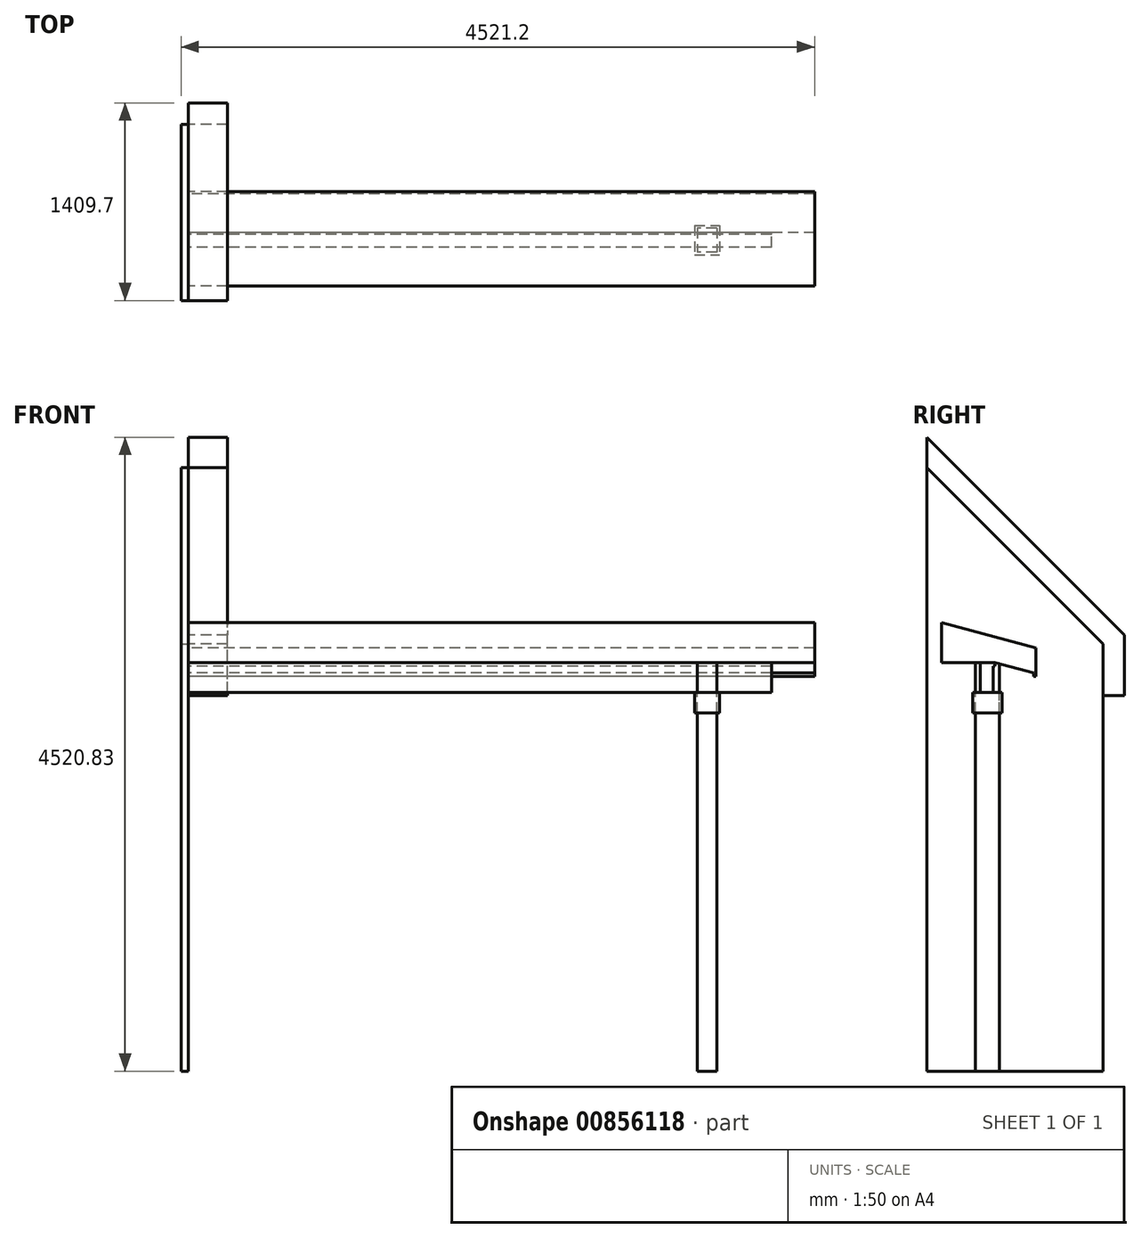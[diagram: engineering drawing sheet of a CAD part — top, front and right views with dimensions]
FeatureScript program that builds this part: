
annotation { "Feature Type Name" : "Feature", "Feature Type Description" : "" }
export const myFeature = defineFeature(function(context is Context, id is Id, definition is map)
    precondition{}
    {
        {
            var Q0;
            Q0=qCreatedBy(makeId("Right.planeOp"),FACE);
            var sketch = newSketch(context, id + "F0", { "sketchPlane" : qUnion([Q0])});
            skLineSegment(sketch, "E0.bottom", {"start": v(0, 2701.93) * mm, "end": v(92.07, 2701.93) * mm});
            skLineSegment(sketch, "E0.top", {"start": v(0, 2914.65) * mm, "end": v(104.77, 2914.65) * mm});
            skLineSegment(sketch, "E0.left", {"start": v(0, 2701.93) * mm, "end": v(0, 2914.65) * mm});
            skLineSegment(sketch, "E0.right", {"start": v(92.07, 2701.93) * mm, "end": v(92.07, 2889.25) * mm});
            skLineSegment(sketch, "E1", {"start": v(92.07, 2889.25) * mm, "end": v(104.77, 2889.25) * mm});
            skLineSegment(sketch, "E2", {"start": v(104.77, 2889.25) * mm, "end": v(104.77, 2889.25) * mm});
            skLineSegment(sketch, "E3", {"start": v(104.77, 2889.25) * mm, "end": v(104.77, 2914.65) * mm});
            skSolve(sketch);
        }
        {
            var Q0;
            Q0 = qSketchRegion(id + "F0", true);
            extrude(context, id + "F1", {"entities" : qUnion([Q0]), "depth" : 4162.43 * mm, "offsetDistance" : 25.4 * mm});
        }
        {
            var Q0;
            Q0=makeQuery(id+"F1.opExtrude","SWEPT_FACE",FACE,{"disambiguationData":[OSD([sQuery(id+"F0.wireOp",EDGE,"E0.top")])]});
            var sketch = newSketch(context, id + "F2", { "sketchPlane" : qUnion([Q0])});
            skLineSegment(sketch, "E4.bottom", {"start": v(3632.2, -34.93) * mm, "end": v(3771.9, -34.93) * mm});
            skLineSegment(sketch, "E4.top", {"start": v(3632.2, 136.52) * mm, "end": v(3771.9, 136.52) * mm});
            skLineSegment(sketch, "E4.left", {"start": v(3632.2, -34.93) * mm, "end": v(3632.2, 136.52) * mm});
            skLineSegment(sketch, "E4.right", {"start": v(3771.9, -34.93) * mm, "end": v(3771.9, 136.52) * mm});
            skSolve(sketch);
        }
        {
            var Q0;
            Q0 = qSketchRegion(id + "F2", true);
            var Q1;
            Q1=qCreatedBy(makeId("Top.planeOp"),FACE);
            extrude(context, id + "F3", {"entities" : qUnion([Q0]), "endBound" : BoundingType.UP_TO_SURFACE, "oppositeDirection" : true, "depth" : 25.4 * mm, "endBoundEntityFace" : qUnion([Q1]), "offsetDistance" : 25.4 * mm});
        }
        {
            var Q0;
            Q0=qCreatedBy(makeId("Right.planeOp"),FACE);
            var sketch = newSketch(context, id + "F4", { "sketchPlane" : qUnion([Q0])});
            skLineSegment(sketch, "E5", {"start": v(104.77, 2914.65) * mm, "end": v(380.79, 2840.7) * mm});
            skLineSegment(sketch, "E6", {"start": v(380.79, 2840.7) * mm, "end": v(380.79, 2815.3) * mm});
            skLineSegment(sketch, "E7", {"start": v(380.79, 2815.3) * mm, "end": v(396.66, 2815.3) * mm});
            skLineSegment(sketch, "E8", {"start": v(396.66, 2815.3) * mm, "end": v(396.66, 3018.5) * mm});
            skLineSegment(sketch, "E9", {"start": v(396.66, 3018.5) * mm, "end": v(-276.23, 3198.8) * mm});
            skLineSegment(sketch, "E10", {"start": v(-276.23, 2914.65) * mm, "end": v(104.77, 2914.65) * mm});
            skLineSegment(sketch, "E11", {"start": v(-276.23, 3198.8) * mm, "end": v(-276.23, 2914.65) * mm});
            skSolve(sketch);
        }
        {
            var Q0;
            Q0 = qSketchRegion(id + "F4", true);
            extrude(context, id + "F5", {"entities" : qUnion([Q0]), "depth" : 4470.4 * mm, "offsetDistance" : 25.4 * mm});
        }
        {
            var Q0;
            Q0=makeQuery(id+"F1.opExtrude","SWEPT_FACE",FACE,{"disambiguationData":[OSD([sQuery(id+"F0.wireOp",EDGE,"E0.bottom")])]});
            var sketch = newSketch(context, id + "F6", { "sketchPlane" : qUnion([Q0])});
            skLineSegment(sketch, "E12.bottom", {"start": v(3613.15, -155.57) * mm, "end": v(3790.95, -155.57) * mm});
            skLineSegment(sketch, "E12.top", {"start": v(3613.15, 53.98) * mm, "end": v(3790.95, 53.98) * mm});
            skLineSegment(sketch, "E12.left", {"start": v(3613.15, -155.57) * mm, "end": v(3613.15, 53.98) * mm});
            skLineSegment(sketch, "E12.right", {"start": v(3790.95, -155.57) * mm, "end": v(3790.95, 53.98) * mm});
            skSolve(sketch);
        }
        {
            var Q0;
            Q0 = qSketchRegion(id + "F6", true);
            extrude(context, id + "F7", {"entities" : qUnion([Q0]), "depth" : 147.32 * mm, "offsetDistance" : 25.4 * mm});
        }
        {
            var Q0;
            Q0=qCreatedBy(makeId("Right.planeOp"),FACE);
            var sketch = newSketch(context, id + "F8", { "sketchPlane" : qUnion([Q0])});
            skLineSegment(sketch, "E13", {"start": v(876.3, 0) * mm, "end": v(876.3, 3048) * mm});
            skLineSegment(sketch, "E14", {"start": v(876.3, 3048) * mm, "end": v(-381, 4305.3) * mm});
            skLineSegment(sketch, "E15", {"start": v(-381, 4305.3) * mm, "end": v(-381, 0) * mm});
            skLineSegment(sketch, "E16", {"start": v(-381, 0) * mm, "end": v(876.3, 0) * mm});
            skSolve(sketch);
        }
        {
            var Q0;
            Q0 = qSketchRegion(id + "F8", true);
            extrude(context, id + "F9", {"entities" : qUnion([Q0]), "oppositeDirection" : true, "depth" : 50.8 * mm, "offsetDistance" : 25.4 * mm});
        }
        {
            var Q0;
            Q0=makeQuery(id+"F9.opExtrude","CAP_FACE",FACE,{"disambiguationData":[OSD([sQuery(id+"F8.wireOp",EDGE,"E13"),sQuery(id+"F8.wireOp",EDGE,"E14"),sQuery(id+"F8.wireOp",EDGE,"E15"),sQuery(id+"F8.wireOp",EDGE,"E16")])],"isStart":true});
            var sketch = newSketch(context, id + "F10", { "sketchPlane" : qUnion([Q0])});
            skLineSegment(sketch, "E17", {"start": v(876.3, 2679.7) * mm, "end": v(1028.7, 2679.7) * mm});
            skLineSegment(sketch, "E18", {"start": v(1028.7, 2679.7) * mm, "end": v(1028.7, 3111.13) * mm});
            skLineSegment(sketch, "E19", {"start": v(-381, 4305.3) * mm, "end": v(876.3, 3048) * mm});
            skLineSegment(sketch, "E20", {"start": v(876.3, 3048) * mm, "end": v(876.3, 2679.7) * mm});
            skLineSegment(sketch, "E21", {"start": v(-381, 4305.3) * mm, "end": v(-381, 4520.83) * mm});
            skLineSegment(sketch, "E22", {"start": v(-381, 4520.83) * mm, "end": v(1028.7, 3111.13) * mm});
            skSolve(sketch);
        }
        {
            var Q0;
            Q0 = qSketchRegion(id + "F10", true);
            extrude(context, id + "F11", {"entities" : qUnion([Q0]), "depth" : 279.4 * mm, "offsetDistance" : 25.4 * mm});
        }
    });
